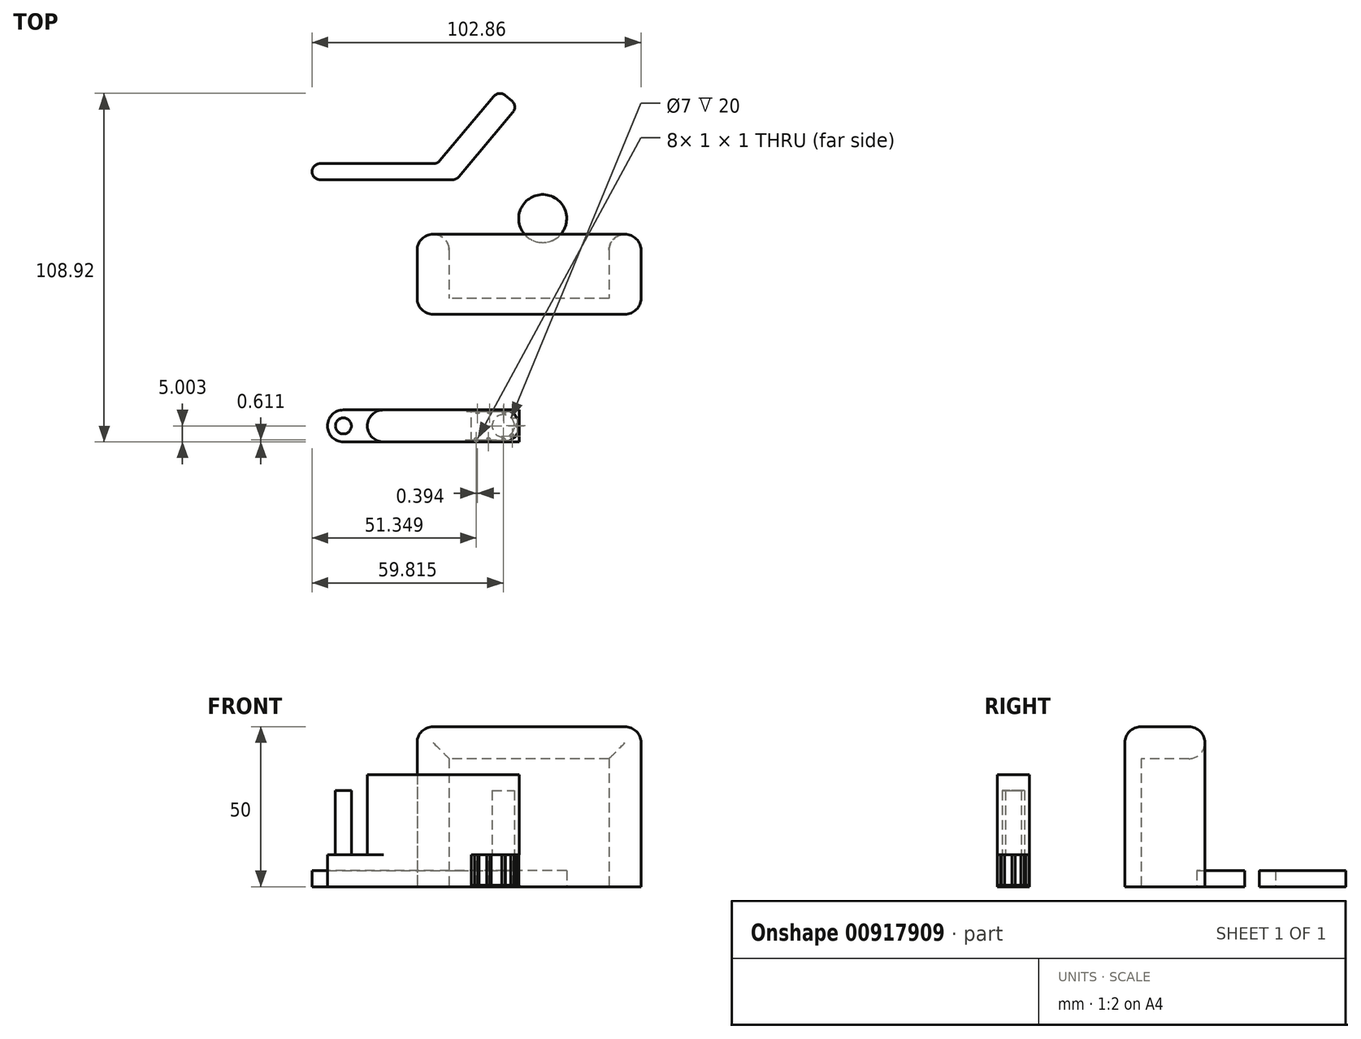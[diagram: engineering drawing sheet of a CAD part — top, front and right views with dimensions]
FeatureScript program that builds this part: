
annotation { "Feature Type Name" : "Feature", "Feature Type Description" : "" }
export const myFeature = defineFeature(function(context is Context, id is Id, definition is map)
    precondition{}
    {
        {
            var Q0;
            Q0=qCreatedBy(makeId("Top.planeOp"),FACE);
            var sketch = newSketch(context, id + "F0", { "sketchPlane" : qUnion([Q0])});
            skLineSegment(sketch, "E0", {"start": v(-67.86, 29.56) * mm, "end": v(-22.74, 29.56) * mm});
            skLineSegment(sketch, "E1", {"start": v(-22.74, 29.56) * mm, "end": v(-3.46, 52.54) * mm});
            skLineSegment(sketch, "E2", {"start": v(-3.46, 52.54) * mm, "end": v(-9.42, 57.54) * mm});
            skLineSegment(sketch, "E3", {"start": v(-22.74, 29.56) * mm, "end": v(-28.7, 34.56) * mm});
            skLineSegment(sketch, "E4", {"start": v(-9.42, 57.54) * mm, "end": v(-28.7, 34.56) * mm});
            skLineSegment(sketch, "E5", {"start": v(-28.7, 34.56) * mm, "end": v(-67.86, 34.56) * mm});
            skLineSegment(sketch, "E6", {"start": v(-67.86, 34.56) * mm, "end": v(-67.86, 29.56) * mm});
            skCircle(sketch, "E7", {"center": v(4.26, 17.4) * mm, "radius": 7.5 * mm});
            skLineSegment(sketch, "E8.bottom", {"start": v(35, -12.5) * mm, "end": v(-35, -12.5) * mm});
            skLineSegment(sketch, "E8.left", {"start": v(35, -12.5) * mm, "end": v(35, 12.5) * mm});
            skLineSegment(sketch, "E8.right", {"start": v(-35, -12.5) * mm, "end": v(-35, 12.5) * mm});
            skPoint(sketch, "E8.middle", {"position": v(0, 0) * mm});
            skLineSegment(sketch, "E9", {"start": v(-35, 12.5) * mm, "end": v(-25, 12.5) * mm});
            skLineSegment(sketch, "E10", {"start": v(-25, 12.5) * mm, "end": v(-25, -7.5) * mm});
            skLineSegment(sketch, "E11", {"start": v(-25, -7.5) * mm, "end": v(25, -7.5) * mm});
            skLineSegment(sketch, "E12", {"start": v(25, -7.5) * mm, "end": v(25, 12.5) * mm});
            skLineSegment(sketch, "E13", {"start": v(25, 12.5) * mm, "end": v(35, 12.5) * mm});
            skLineSegment(sketch, "E14.bottom", {"start": v(-63.05, -42.4) * mm, "end": v(-3.05, -42.4) * mm});
            skLineSegment(sketch, "E14.top", {"start": v(-63.05, -52.4) * mm, "end": v(-3.05, -52.4) * mm});
            skLineSegment(sketch, "E14.left", {"start": v(-63.05, -42.4) * mm, "end": v(-63.05, -52.4) * mm});
            skLineSegment(sketch, "E14.right", {"start": v(-3.05, -42.4) * mm, "end": v(-3.05, -52.4) * mm});
            skLineSegment(sketch, "E15", {"start": v(-44.58, -52.4) * mm, "end": v(-44.58, -42.4) * mm});
            skSolve(sketch);
        }
        {
            var Q0;
            Q0=makeQuery(id+"F0.imprint","IMPRINT",FACE,{"disambiguationData":[TD([[makeQuery(id+"F0.imprint","IMPRINT",EDGE,{"derivedFrom":sQuery(id+"F0.wireOp",EDGE,"E0")}),1.0]])]});
            var Q1;
            Q1=makeQuery(id+"F0.imprint","IMPRINT",FACE,{"disambiguationData":[TD([[makeQuery(id+"F0.imprint","IMPRINT",EDGE,{"derivedFrom":sQuery(id+"F0.wireOp",EDGE,"E1")}),1.0]])]});
            var Q2;
            Q2=makeQuery(id+"F0.imprint","IMPRINT",FACE,{"disambiguationData":[TD([[makeQuery(id+"F0.imprint","IMPRINT",EDGE,{"derivedFrom":sQuery(id+"F0.wireOp",EDGE,"E7")}),1.0]])]});
            extrude(context, id + "F1", {"entities" : qUnion([Q0, Q1, Q2]), "depth" : 5 * mm, "offsetDistance" : 25 * mm});
        }
        {
            var Q0;
            Q0=makeQuery(id+"F1.opExtrude","SWEPT_EDGE",EDGE,{"disambiguationData":[OSD([sQuery(id+"F0.wireOp",EDGE,"E3"),sQuery(id+"F0.wireOp",EDGE,"E4"),sQuery(id+"F0.wireOp",EDGE,"E5")])]});
            var Q1;
            Q1=makeQuery(id+"F1.opExtrude","SWEPT_EDGE",EDGE,{"disambiguationData":[OSD([sQuery(id+"F0.wireOp",EDGE,"E5"),sQuery(id+"F0.wireOp",EDGE,"E6")])]});
            var Q2;
            Q2=makeQuery(id+"F1.opExtrude","SWEPT_EDGE",EDGE,{"disambiguationData":[OSD([sQuery(id+"F0.wireOp",EDGE,"E0"),sQuery(id+"F0.wireOp",EDGE,"E6")])]});
            var Q3;
            Q3=makeQuery(id+"F1.opExtrude","SWEPT_EDGE",EDGE,{"disambiguationData":[OSD([sQuery(id+"F0.wireOp",EDGE,"E0"),sQuery(id+"F0.wireOp",EDGE,"E1"),sQuery(id+"F0.wireOp",EDGE,"E3")])]});
            var Q4;
            Q4=makeQuery(id+"F1.opExtrude","SWEPT_EDGE",EDGE,{"disambiguationData":[OSD([sQuery(id+"F0.wireOp",EDGE,"E1"),sQuery(id+"F0.wireOp",EDGE,"E2")])]});
            var Q5;
            Q5=makeQuery(id+"F1.opExtrude","SWEPT_EDGE",EDGE,{"disambiguationData":[OSD([sQuery(id+"F0.wireOp",EDGE,"E2"),sQuery(id+"F0.wireOp",EDGE,"E4")])]});
            fillet(context, id + "F2", {"entities" : qUnion([Q0, Q1, Q2, Q3, Q4, Q5]), "radius" : 2.5 * mm, "tangentPropagation" : true, "allowEdgeOverflow" : false});
        }
        {
            var Q0;
            Q0=makeQuery(id+"F0.imprint","IMPRINT",FACE,{"disambiguationData":[TD([[makeQuery(id+"F0.imprint","IMPRINT",EDGE,{"derivedFrom":sQuery(id+"F0.wireOp",EDGE,"E8.bottom")}),-1.0]])]});
            extrude(context, id + "F3", {"entities" : qUnion([Q0]), "depth" : 50 * mm, "offsetDistance" : 25 * mm});
        }
        {
            var Q0;
            Q0=makeQuery(id+"F3.opExtrude","SWEPT_FACE",FACE,{"disambiguationData":[OSD([sQuery(id+"F0.wireOp",EDGE,"E11")])]});
            var sketch = newSketch(context, id + "F4", { "sketchPlane" : qUnion([Q0])});
            skLineSegment(sketch, "E16.0", {"start": v(-25, 50) * mm, "end": v(-25, 0) * mm});
            skLineSegment(sketch, "E17.0", {"start": v(25, 0) * mm, "end": v(25, 50) * mm});
            skLineSegment(sketch, "E18.bottom", {"start": v(-25, 50) * mm, "end": v(25, 50) * mm});
            skLineSegment(sketch, "E18.left", {"start": v(-25, 50) * mm, "end": v(-25, 40) * mm});
            skLineSegment(sketch, "E18.right", {"start": v(25, 50) * mm, "end": v(25, 40) * mm});
            skLineSegment(sketch, "E19.0", {"start": v(25, 50) * mm, "end": v(25, 0) * mm});
            skLineSegment(sketch, "E20.top", {"start": v(-25, 40) * mm, "end": v(25, 40) * mm});
            skSolve(sketch);
        }
        {
            var Q0;
            Q0=makeQuery(id+"F4.imprint","IMPRINT",FACE,{"disambiguationData":[TD([[makeQuery(id+"F4.imprint","IMPRINT",EDGE,{"derivedFrom":sQuery(id+"F4.wireOp",EDGE,"E18.bottom")}),1.0]])]});
            extrude(context, id + "F5", {"entities" : qUnion([Q0]), "operationType" : NewBodyOperationType.ADD, "depth" : 20 * mm, "offsetDistance" : 25 * mm});
        }
        {
            var Q0;
            Q0=makeQuery(id+"F5.opExtrude","CAP_EDGE",EDGE,{"disambiguationData":[OSD([sQuery(id+"F4.wireOp",EDGE,"E20.top")])],"isStart":false});
            var Q1;
            Q1=makeQuery(id+"F3.opExtrude","SWEPT_EDGE",EDGE,{"disambiguationData":[OSD([sQuery(id+"F0.wireOp",EDGE,"E12"),sQuery(id+"F0.wireOp",EDGE,"E13")])]});
            var Q2;
            Q2=makeQuery(id+"F3.opExtrude","SWEPT_EDGE",EDGE,{"disambiguationData":[OSD([sQuery(id+"F0.wireOp",EDGE,"E9"),sQuery(id+"F0.wireOp",EDGE,"E10")])]});
            var Q3;
            Q3=makeQuery(id+"F5.boolean.opBoolean","MERGE",EDGE,{"derivedFrom":[makeQuery(id+"F3.opExtrude","CAP_EDGE",EDGE,{"disambiguationData":[OSD([sQuery(id+"F0.wireOp",EDGE,"E9")])],"isStart":false}),makeQuery(id+"F3.opExtrude","CAP_EDGE",EDGE,{"disambiguationData":[OSD([sQuery(id+"F0.wireOp",EDGE,"E13")])],"isStart":false}),makeQuery(id+"F5.opExtrude","CAP_EDGE",EDGE,{"disambiguationData":[OSD([sQuery(id+"F4.wireOp",EDGE,"E18.bottom")])],"isStart":false})]});
            var Q4;
            Q4=makeQuery(id+"F3.opExtrude","SWEPT_EDGE",EDGE,{"disambiguationData":[OSD([sQuery(id+"F0.wireOp",EDGE,"E8.left"),sQuery(id+"F0.wireOp",EDGE,"E13")])]});
            var Q5;
            Q5=makeQuery(id+"F3.opExtrude","SWEPT_EDGE",EDGE,{"disambiguationData":[OSD([sQuery(id+"F0.wireOp",EDGE,"E8.right"),sQuery(id+"F0.wireOp",EDGE,"E9")])]});
            var Q6;
            Q6=makeQuery(id+"F3.opExtrude","CAP_EDGE",EDGE,{"disambiguationData":[OSD([sQuery(id+"F0.wireOp",EDGE,"E8.right")])],"isStart":false});
            var Q7;
            Q7=makeQuery(id+"F3.opExtrude","CAP_EDGE",EDGE,{"disambiguationData":[OSD([sQuery(id+"F0.wireOp",EDGE,"E8.left")])],"isStart":false});
            var Q8;
            Q8=makeQuery(id+"F3.opExtrude","CAP_EDGE",EDGE,{"disambiguationData":[OSD([sQuery(id+"F0.wireOp",EDGE,"E8.bottom")])],"isStart":false});
            var Q9;
            Q9=makeQuery(id+"F3.opExtrude","SWEPT_EDGE",EDGE,{"disambiguationData":[OSD([sQuery(id+"F0.wireOp",EDGE,"E8.bottom"),sQuery(id+"F0.wireOp",EDGE,"E8.left")])]});
            var Q10;
            Q10=makeQuery(id+"F3.opExtrude","SWEPT_EDGE",EDGE,{"disambiguationData":[OSD([sQuery(id+"F0.wireOp",EDGE,"E8.bottom"),sQuery(id+"F0.wireOp",EDGE,"E8.right")])]});
            fillet(context, id + "F6", {"entities" : qUnion([Q0, Q1, Q2, Q3, Q4, Q5, Q6, Q7, Q8, Q9, Q10]), "radius" : 5 * mm, "tangentPropagation" : true, "allowEdgeOverflow" : false});
        }
        {
            var Q0;
            Q0=makeQuery(id+"F0.imprint","IMPRINT",FACE,{"disambiguationData":[TD([[makeQuery(id+"F0.imprint","IMPRINT",EDGE,{"derivedFrom":sQuery(id+"F0.wireOp",EDGE,"E14.bottom")}),-1.0]])]});
            extrude(context, id + "F7", {"entities" : qUnion([Q0]), "depth" : 10 * mm, "offsetDistance" : 25 * mm});
        }
        {
            var Q0;
            Q0=makeQuery(id+"F7.opExtrude","CAP_FACE",FACE,{"disambiguationData":[OSD([sQuery(id+"F0.wireOp",EDGE,"E14.bottom"),sQuery(id+"F0.wireOp",EDGE,"E14.top"),sQuery(id+"F0.wireOp",EDGE,"E14.left"),sQuery(id+"F0.wireOp",EDGE,"E14.right")])],"isStart":false});
            var sketch = newSketch(context, id + "F8", { "sketchPlane" : qUnion([Q0])});
            skCircle(sketch, "E21", {"center": v(-58.05, -47.4) * mm, "radius": 2.5 * mm});
            skPoint(sketch, "E21.centerSnap0", {"position": v(-63.05, -47.4) * mm});
            skLineSegment(sketch, "E22", {"start": v(-50.55, -42.4) * mm, "end": v(-50.55, -52.4) * mm});
            skSolve(sketch);
        }
        {
            var Q0;
            {var subQ0=sQuery(id+"F8.wireOp",EDGE,"E22");Q0=makeQuery(id+"F8.imprint","IMPRINT",FACE,{"disambiguationData":[TD([[makeQuery(id+"F8.imprint","IMPRINT",EDGE,{"derivedFrom":subQ0}),1.0]])]});}
            extrude(context, id + "F9", {"entities" : qUnion([Q0]), "operationType" : NewBodyOperationType.ADD, "depth" : 25 * mm, "offsetDistance" : 25 * mm});
        }
        {
            var Q0;
            {var subQ0=sQuery(id+"F0.wireOp",EDGE,"E14.right");Q0=makeQuery(id+"F9.boolean.opBoolean","MERGE",FACE,{"derivedFrom":[makeQuery(id+"F7.opExtrude","SWEPT_FACE",FACE,{"disambiguationData":[OSD([subQ0])]}),makeQuery(id+"F9.opExtrude","SWEPT_FACE",FACE,{"disambiguationData":[OSD([subQ0])]})]});}
            var sketch = newSketch(context, id + "F10", { "sketchPlane" : qUnion([Q0])});
            skLineSegment(sketch, "E23", {"start": v(-52.4, 10) * mm, "end": v(-42.4, 10) * mm});
            skSolve(sketch);
        }
        {
            var Q0;
            {var subQ0=sQuery(id+"F10.wireOp",EDGE,"E23");Q0=makeQuery(id+"F10.imprint","IMPRINT",FACE,{"disambiguationData":[TD([[makeQuery(id+"F10.imprint","IMPRINT",EDGE,{"derivedFrom":subQ0}),-1.0]])]});}
            extrude(context, id + "F11", {"entities" : qUnion([Q0]), "operationType" : NewBodyOperationType.REMOVE, "oppositeDirection" : true, "depth" : 15 * mm, "offsetDistance" : 25 * mm});
        }
        {
            var Q0;
            Q0=makeQuery(id+"F11.boolean.opBoolean","COPY",FACE,{"derivedFrom":makeQuery(id+"F11.opExtrude","SWEPT_FACE",FACE,{"disambiguationData":[OSD([sQuery(id+"F10.wireOp",EDGE,"E23")])]})});
            var sketch = newSketch(context, id + "F12", { "sketchPlane" : qUnion([Q0])});
            skCircle(sketch, "E24", {"center": v(-8.05, 47.4) * mm, "radius": 3.5 * mm});
            skPoint(sketch, "E24.centerSnap0", {"position": v(-10.55, 52.4) * mm});
            skPoint(sketch, "E24.centerSnap1", {"position": v(-3.05, 47.4) * mm});
            skSolve(sketch);
        }
        {
            var Q0;
            Q0=makeQuery(id+"F12.imprint","IMPRINT",FACE,{"disambiguationData":[TD([[makeQuery(id+"F12.imprint","IMPRINT",EDGE,{"derivedFrom":sQuery(id+"F12.wireOp",EDGE,"E24")}),1.0]])]});
            extrude(context, id + "F13", {"entities" : qUnion([Q0]), "operationType" : NewBodyOperationType.REMOVE, "oppositeDirection" : true, "depth" : 20 * mm, "offsetDistance" : 25 * mm});
        }
        {
            var Q0;
            Q0=makeQuery(id+"F8.imprint","IMPRINT",FACE,{"disambiguationData":[TD([[makeQuery(id+"F8.imprint","IMPRINT",EDGE,{"derivedFrom":sQuery(id+"F8.wireOp",EDGE,"E21")}),1.0]])]});
            extrude(context, id + "F14", {"entities" : qUnion([Q0]), "operationType" : NewBodyOperationType.ADD, "depth" : 20 * mm, "offsetDistance" : 25 * mm});
        }
        {
            var Q0;
            Q0=makeQuery(id+"F9.opExtrude","SWEPT_EDGE",EDGE,{"disambiguationData":[OSD([sQuery(id+"F0.wireOp",EDGE,"E14.top"),sQuery(id+"F8.wireOp",EDGE,"E22")])]});
            var Q1;
            Q1=makeQuery(id+"F9.opExtrude","SWEPT_EDGE",EDGE,{"disambiguationData":[OSD([sQuery(id+"F0.wireOp",EDGE,"E14.bottom"),sQuery(id+"F8.wireOp",EDGE,"E22")])]});
            var Q2;
            Q2=makeQuery(id+"F7.opExtrude","SWEPT_EDGE",EDGE,{"disambiguationData":[OSD([sQuery(id+"F0.wireOp",EDGE,"E14.top"),sQuery(id+"F0.wireOp",EDGE,"E14.left")])]});
            var Q3;
            Q3=makeQuery(id+"F7.opExtrude","SWEPT_EDGE",EDGE,{"disambiguationData":[OSD([sQuery(id+"F0.wireOp",EDGE,"E14.bottom"),sQuery(id+"F0.wireOp",EDGE,"E14.left")])]});
            var Q4;
            {var subQ0=sQuery(id+"F0.wireOp",EDGE,"E14.right");var subQ1=sQuery(id+"F0.wireOp",EDGE,"E14.bottom");Q4=makeQuery(id+"F9.boolean.opBoolean","MERGE",EDGE,{"derivedFrom":[makeQuery(id+"F7.opExtrude","SWEPT_EDGE",EDGE,{"disambiguationData":[OSD([subQ1,subQ0])]}),makeQuery(id+"F9.opExtrude","SWEPT_EDGE",EDGE,{"disambiguationData":[OSD([subQ1,subQ0])]})]});}
            var Q5;
            {var subQ0=sQuery(id+"F0.wireOp",EDGE,"E14.right");var subQ1=sQuery(id+"F0.wireOp",EDGE,"E14.top");Q5=makeQuery(id+"F9.boolean.opBoolean","MERGE",EDGE,{"derivedFrom":[makeQuery(id+"F7.opExtrude","SWEPT_EDGE",EDGE,{"disambiguationData":[OSD([subQ1,subQ0])]}),makeQuery(id+"F9.opExtrude","SWEPT_EDGE",EDGE,{"disambiguationData":[OSD([subQ1,subQ0])]})]});}
            var Q6;
            Q6=makeQuery(id+"F11.boolean.opBoolean","COPY",EDGE,{"derivedFrom":makeQuery(id+"F11.opExtrude","CAP_EDGE",EDGE,{"disambiguationData":[OSD([sQuery(id+"F0.wireOp",EDGE,"E14.top"),sQuery(id+"F0.wireOp",EDGE,"E14.right")])],"isStart":false})});
            var Q7;
            Q7=makeQuery(id+"F11.boolean.opBoolean","COPY",EDGE,{"derivedFrom":makeQuery(id+"F11.opExtrude","CAP_EDGE",EDGE,{"disambiguationData":[OSD([sQuery(id+"F0.wireOp",EDGE,"E14.bottom"),sQuery(id+"F0.wireOp",EDGE,"E14.right")])],"isStart":false})});
            fillet(context, id + "F15", {"entities" : qUnion([Q0, Q1, Q2, Q3, Q4, Q5, Q6, Q7]), "radius" : 5 * mm, "tangentPropagation" : true, "allowEdgeOverflow" : false});
        }
        {
            var Q0;
            Q0=makeQuery(id+"F11.boolean.opBoolean","COPY",FACE,{"derivedFrom":makeQuery(id+"F11.opExtrude","SWEPT_FACE",FACE,{"disambiguationData":[OSD([sQuery(id+"F10.wireOp",EDGE,"E23")])]})});
            var sketch = newSketch(context, id + "F16", { "sketchPlane" : qUnion([Q0])});
            skLineSegment(sketch, "E25.bottom", {"start": v(-3.15, 46.85) * mm, "end": v(-4.15, 46.85) * mm});
            skLineSegment(sketch, "E25.top", {"start": v(-3.15, 47.85) * mm, "end": v(-4.15, 47.85) * mm});
            skLineSegment(sketch, "E25.left", {"start": v(-3.15, 46.85) * mm, "end": v(-3.15, 47.85) * mm});
            skLineSegment(sketch, "E25.right", {"start": v(-4.15, 46.85) * mm, "end": v(-4.15, 47.85) * mm});
            skPoint(sketch, "E25.middle", {"position": v(-3.65, 47.35) * mm});
            skLineSegment(sketch, "E26.bottom", {"start": v(-7.45, 42.5) * mm, "end": v(-8.45, 42.5) * mm});
            skLineSegment(sketch, "E26.top", {"start": v(-7.45, 43.5) * mm, "end": v(-8.45, 43.5) * mm});
            skLineSegment(sketch, "E26.left", {"start": v(-7.45, 42.5) * mm, "end": v(-7.45, 43.5) * mm});
            skLineSegment(sketch, "E26.right", {"start": v(-8.45, 42.5) * mm, "end": v(-8.45, 43.5) * mm});
            skPoint(sketch, "E26.middle", {"position": v(-7.95, 43) * mm});
            skLineSegment(sketch, "E27.bottom", {"start": v(-7.56, 51.34) * mm, "end": v(-8.56, 51.34) * mm});
            skLineSegment(sketch, "E27.top", {"start": v(-7.56, 52.34) * mm, "end": v(-8.56, 52.34) * mm});
            skLineSegment(sketch, "E27.left", {"start": v(-7.56, 51.34) * mm, "end": v(-7.56, 52.34) * mm});
            skLineSegment(sketch, "E27.right", {"start": v(-8.56, 51.34) * mm, "end": v(-8.56, 52.34) * mm});
            skPoint(sketch, "E27.middle", {"position": v(-8.06, 51.84) * mm});
            skLineSegment(sketch, "E28.bottom", {"start": v(-4.38, 45) * mm, "end": v(-5.38, 45) * mm});
            skLineSegment(sketch, "E28.top", {"start": v(-4.38, 44) * mm, "end": v(-5.38, 44) * mm});
            skLineSegment(sketch, "E28.left", {"start": v(-4.38, 45) * mm, "end": v(-4.38, 44) * mm});
            skLineSegment(sketch, "E28.right", {"start": v(-5.38, 45) * mm, "end": v(-5.38, 44) * mm});
            skPoint(sketch, "E28.middle", {"position": v(-4.88, 44.5) * mm});
            skLineSegment(sketch, "E29.bottom", {"start": v(-4.72, 51.14) * mm, "end": v(-5.72, 51.14) * mm});
            skLineSegment(sketch, "E29.top", {"start": v(-4.72, 50.14) * mm, "end": v(-5.72, 50.14) * mm});
            skLineSegment(sketch, "E29.left", {"start": v(-4.72, 51.14) * mm, "end": v(-4.72, 50.14) * mm});
            skLineSegment(sketch, "E29.right", {"start": v(-5.72, 51.14) * mm, "end": v(-5.72, 50.14) * mm});
            skPoint(sketch, "E29.middle", {"position": v(-5.22, 50.64) * mm});
            skLineSegment(sketch, "E30.bottom", {"start": v(-11.89, 43.47) * mm, "end": v(-12.89, 43.47) * mm});
            skLineSegment(sketch, "E30.top", {"start": v(-11.89, 42.47) * mm, "end": v(-12.89, 42.47) * mm});
            skLineSegment(sketch, "E30.left", {"start": v(-11.89, 43.47) * mm, "end": v(-11.89, 42.47) * mm});
            skLineSegment(sketch, "E30.right", {"start": v(-12.89, 43.47) * mm, "end": v(-12.89, 42.47) * mm});
            skPoint(sketch, "E30.middle", {"position": v(-12.39, 42.97) * mm});
            skLineSegment(sketch, "E31.bottom", {"start": v(-12.23, 51.29) * mm, "end": v(-13.23, 51.29) * mm});
            skLineSegment(sketch, "E31.top", {"start": v(-12.23, 52.29) * mm, "end": v(-13.23, 52.29) * mm});
            skLineSegment(sketch, "E31.left", {"start": v(-12.23, 51.29) * mm, "end": v(-12.23, 52.29) * mm});
            skLineSegment(sketch, "E31.right", {"start": v(-13.23, 51.29) * mm, "end": v(-13.23, 52.29) * mm});
            skPoint(sketch, "E31.middle", {"position": v(-12.73, 51.79) * mm});
            skLineSegment(sketch, "E32.bottom", {"start": v(-16.01, 52.29) * mm, "end": v(-17.01, 52.29) * mm});
            skLineSegment(sketch, "E32.top", {"start": v(-16.01, 51.29) * mm, "end": v(-17.01, 51.29) * mm});
            skLineSegment(sketch, "E32.left", {"start": v(-16.01, 52.29) * mm, "end": v(-16.01, 51.29) * mm});
            skLineSegment(sketch, "E32.right", {"start": v(-17.01, 52.29) * mm, "end": v(-17.01, 51.29) * mm});
            skPoint(sketch, "E32.middle", {"position": v(-16.51, 51.79) * mm});
            skLineSegment(sketch, "E33.bottom", {"start": v(-15.62, 42.5) * mm, "end": v(-16.62, 42.5) * mm});
            skLineSegment(sketch, "E33.top", {"start": v(-15.62, 43.5) * mm, "end": v(-16.62, 43.5) * mm});
            skLineSegment(sketch, "E33.left", {"start": v(-15.62, 42.5) * mm, "end": v(-15.62, 43.5) * mm});
            skLineSegment(sketch, "E33.right", {"start": v(-16.62, 42.5) * mm, "end": v(-16.62, 43.5) * mm});
            skPoint(sketch, "E33.middle", {"position": v(-16.12, 43) * mm});
            skSolve(sketch);
        }
        {
            var Q0;
            Q0=makeQuery(id+"F16.imprint","IMPRINT",FACE,{"disambiguationData":[TD([[makeQuery(id+"F16.imprint","IMPRINT",EDGE,{"derivedFrom":sQuery(id+"F16.wireOp",EDGE,"E32.bottom")}),1.0]])]});
            var Q1;
            Q1=makeQuery(id+"F16.imprint","IMPRINT",FACE,{"disambiguationData":[TD([[makeQuery(id+"F16.imprint","IMPRINT",EDGE,{"derivedFrom":sQuery(id+"F16.wireOp",EDGE,"E31.bottom")}),-1.0]])]});
            var Q2;
            Q2=makeQuery(id+"F16.imprint","IMPRINT",FACE,{"disambiguationData":[TD([[makeQuery(id+"F16.imprint","IMPRINT",EDGE,{"derivedFrom":sQuery(id+"F16.wireOp",EDGE,"E27.bottom")}),-1.0]])]});
            var Q3;
            Q3=makeQuery(id+"F16.imprint","IMPRINT",FACE,{"disambiguationData":[TD([[makeQuery(id+"F16.imprint","IMPRINT",EDGE,{"derivedFrom":sQuery(id+"F16.wireOp",EDGE,"E29.bottom")}),1.0]])]});
            var Q4;
            Q4=makeQuery(id+"F16.imprint","IMPRINT",FACE,{"disambiguationData":[TD([[makeQuery(id+"F16.imprint","IMPRINT",EDGE,{"derivedFrom":sQuery(id+"F16.wireOp",EDGE,"E25.bottom")}),-1.0]])]});
            var Q5;
            {var subQ1=sQuery(id+"F16.wireOp",EDGE,"E28.bottom");Q5=makeQuery(id+"F16.imprint","IMPRINT",FACE,{"disambiguationData":[TD([[makeQuery(id+"F16.imprint","IMPRINT",EDGE,{"derivedFrom":subQ1}),1.0]])]});}
            var Q6;
            Q6=makeQuery(id+"F16.imprint","IMPRINT",FACE,{"disambiguationData":[TD([[makeQuery(id+"F16.imprint","IMPRINT",EDGE,{"derivedFrom":sQuery(id+"F16.wireOp",EDGE,"E26.bottom")}),-1.0]])]});
            var Q7;
            Q7=makeQuery(id+"F16.imprint","IMPRINT",FACE,{"disambiguationData":[TD([[makeQuery(id+"F16.imprint","IMPRINT",EDGE,{"derivedFrom":sQuery(id+"F16.wireOp",EDGE,"E30.bottom")}),1.0]])]});
            var Q8;
            Q8=makeQuery(id+"F16.imprint","IMPRINT",FACE,{"disambiguationData":[TD([[makeQuery(id+"F16.imprint","IMPRINT",EDGE,{"derivedFrom":sQuery(id+"F16.wireOp",EDGE,"E33.bottom")}),-1.0]])]});
            extrude(context, id + "F17", {"entities" : qUnion([Q0, Q1, Q2, Q3, Q4, Q5, Q6, Q7, Q8]), "operationType" : NewBodyOperationType.ADD, "depth" : 10 * mm, "offsetDistance" : 25 * mm});
        }
        {
            var Q0;
            {var subQ0=sQuery(id+"F0.wireOp",EDGE,"E14.right");Q0=makeQuery(id+"F0.imprint","IMPRINT",FACE,{"disambiguationData":[TD([[makeQuery(id+"F0.imprint","IMPRINT",EDGE,{"derivedFrom":subQ0}),-1.0]])]});}
            extrude(context, id + "F18", {"entities" : qUnion([Q0]), "operationType" : NewBodyOperationType.ADD, "depth" : 0.5 * mm, "offsetDistance" : 25 * mm});
        }
    });
